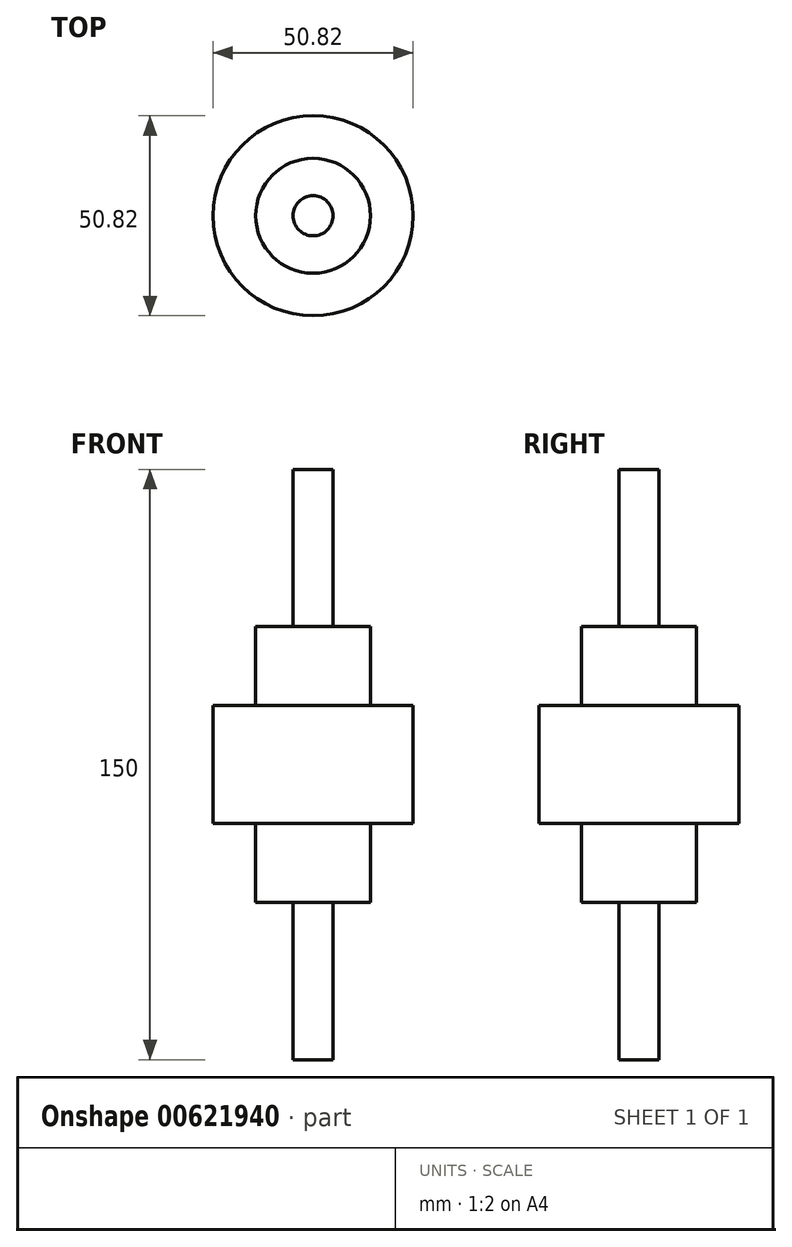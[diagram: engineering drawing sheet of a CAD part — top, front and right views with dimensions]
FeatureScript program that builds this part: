
annotation { "Feature Type Name" : "Feature", "Feature Type Description" : "" }
export const myFeature = defineFeature(function(context is Context, id is Id, definition is map)
    precondition{}
    {
        {
            var Q0;
            Q0=qCreatedBy(makeId("Top.planeOp"),FACE);
            var sketch = newSketch(context, id + "F0", { "sketchPlane" : qUnion([Q0])});
            skCircle(sketch, "E0", {"center": v(0, 0) * mm, "radius": 35.87 * mm});
            skCircle(sketch, "E1", {"center": v(0, 0) * mm, "radius": 25.41 * mm});
            skCircle(sketch, "E2", {"center": v(0, 0) * mm, "radius": 14.59 * mm});
            skCircle(sketch, "E3", {"center": v(0, 0) * mm, "radius": 5.09 * mm});
            skSolve(sketch);
        }
        {
            var Q0;
            Q0=makeQuery(id+"F0.imprint","IMPRINT",FACE,{"disambiguationData":[TD([[makeQuery(id+"F0.imprint","IMPRINT",EDGE,{"derivedFrom":sQuery(id+"F0.wireOp",EDGE,"E3")}),1.0]])]});
            var Q1;
            Q1=sQuery(id+"F0.wireOp",EDGE,"E3");
            extrude(context, id + "F1", {"entities" : qUnion([Q0]), "surfaceEntities" : qUnion([Q1]), "endBound" : BoundingType.SYMMETRIC, "depth" : 150 * mm, "offsetDistance" : 25 * mm});
        }
        {
            var Q0;
            Q0=makeQuery(id+"F0.imprint","IMPRINT",FACE,{"disambiguationData":[TD([[makeQuery(id+"F0.imprint","IMPRINT",EDGE,{"derivedFrom":sQuery(id+"F0.wireOp",EDGE,"E2")}),1.0]])]});
            var Q1;
            Q1=sQuery(id+"F0.wireOp",EDGE,"E2");
            extrude(context, id + "F2", {"entities" : qUnion([Q0]), "operationType" : NewBodyOperationType.ADD, "surfaceEntities" : qUnion([Q1]), "endBound" : BoundingType.SYMMETRIC, "depth" : 70 * mm, "offsetDistance" : 25 * mm});
        }
        {
            var Q0;
            Q0=makeQuery(id+"F0.imprint","IMPRINT",FACE,{"disambiguationData":[TD([[makeQuery(id+"F0.imprint","IMPRINT",EDGE,{"derivedFrom":sQuery(id+"F0.wireOp",EDGE,"E1")}),1.0]])]});
            var Q1;
            Q1=sQuery(id+"F0.wireOp",EDGE,"E1");
            extrude(context, id + "F3", {"entities" : qUnion([Q0]), "operationType" : NewBodyOperationType.ADD, "surfaceEntities" : qUnion([Q1]), "endBound" : BoundingType.SYMMETRIC, "depth" : 30 * mm, "offsetDistance" : 25 * mm});
        }
    });
